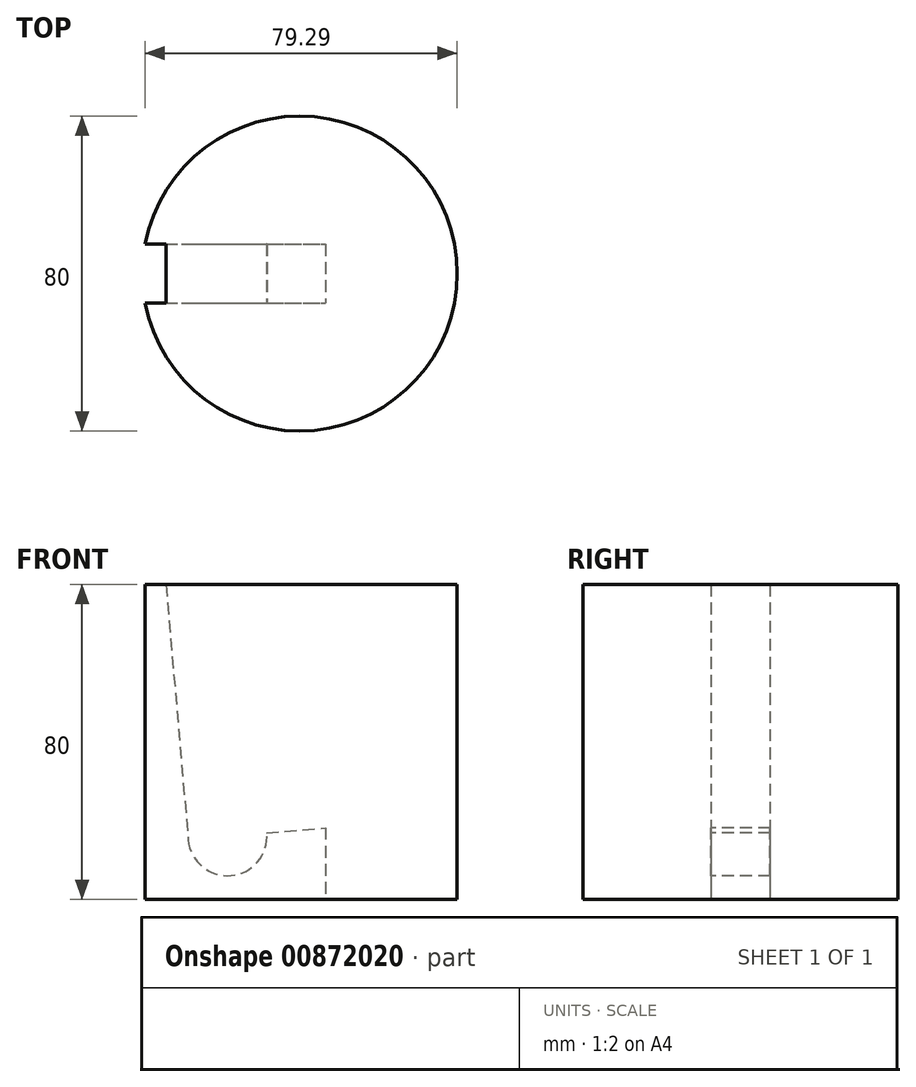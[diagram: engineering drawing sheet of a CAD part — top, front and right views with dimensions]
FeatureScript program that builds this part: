
annotation { "Feature Type Name" : "Feature", "Feature Type Description" : "" }
export const myFeature = defineFeature(function(context is Context, id is Id, definition is map)
    precondition{}
    {
        {
            var Q0;
            Q0=qCreatedBy(makeId("Top.planeOp"),FACE);
            var sketch = newSketch(context, id + "F0", { "sketchPlane" : qUnion([Q0])});
            skCircle(sketch, "E0", {"center": v(0, 0) * mm, "radius": 40 * mm});
            skSolve(sketch);
        }
        {
            var Q0;
            Q0 = qSketchRegion(id + "F0", true);
            extrude(context, id + "F1", {"entities" : qUnion([Q0]), "depth" : 80 * mm, "offsetDistance" : 25 * mm});
        }
        {
            var Q0;
            Q0=qCreatedBy(makeId("Front.planeOp"),FACE);
            var sketch = newSketch(context, id + "F2", { "sketchPlane" : qUnion([Q0])});
            skLineSegment(sketch, "E1", {"start": v(-40, 0) * mm, "end": v(-40, 80) * mm});
            skLineSegment(sketch, "E2.0", {"start": v(-40, 80) * mm, "end": v(40, 80) * mm});
            skLineSegment(sketch, "E3", {"start": v(40, 80) * mm, "end": v(40, 0) * mm});
            skLineSegment(sketch, "E4.0", {"start": v(-40, 0) * mm, "end": v(40, 0) * mm});
            skLineSegment(sketch, "E5", {"start": v(-34, 80) * mm, "end": v(-28.32, 15.13) * mm});
            skArc(sketch, "E6", {"start": v(-28.32, 15.13) * mm, "mid": v(-17.5, 6.04) * mm, "end": v(-8.4, 16.87) * mm});
            skLineSegment(sketch, "E7", {"start": v(-28.32, 15.13) * mm, "end": v(-8.4, 16.87) * mm});
            skLineSegment(sketch, "E8", {"start": v(-8.4, 16.87) * mm, "end": v(6.54, 18.18) * mm});
            skLineSegment(sketch, "E9", {"start": v(6.54, 18.18) * mm, "end": v(6.54, 0) * mm});
            skLineSegment(sketch, "E10", {"start": v(0, 0) * mm, "end": v(0, 80) * mm, "construction": true});
            skLineSegment(sketch, "E11", {"start": v(6.54, 18.18) * mm, "end": v(6.54, 80) * mm});
            skLineSegment(sketch, "E12", {"start": v(6.54, 18.18) * mm, "end": v(40, 18.18) * mm});
            skLineSegment(sketch, "E13", {"start": v(-8.4, 16.87) * mm, "end": v(-10.5, 40.78) * mm});
            skLineSegment(sketch, "E14", {"start": v(-8.57, 18.86) * mm, "end": v(-2.1, 19.43) * mm});
            skLineSegment(sketch, "E15", {"start": v(-2.1, 19.43) * mm, "end": v(-4.02, 41.35) * mm});
            skLineSegment(sketch, "E16", {"start": v(-10.5, 40.78) * mm, "end": v(-4.02, 41.35) * mm});
            skSolve(sketch);
        }
        {
            var Q0;
            {var subQ1=sQuery(id+"F2.wireOp",EDGE,"E1");Q0=makeQuery(id+"F2.imprint","IMPRINT",FACE,{"disambiguationData":[TD([[makeQuery(id+"F2.imprint","IMPRINT",EDGE,{"derivedFrom":subQ1}),-1.0]])]});}
            extrude(context, id + "F3", {"entities" : qUnion([Q0]), "operationType" : NewBodyOperationType.REMOVE, "endBound" : BoundingType.SYMMETRIC, "oppositeDirection" : true, "depth" : 15 * mm, "offsetDistance" : 25 * mm});
        }
    });
